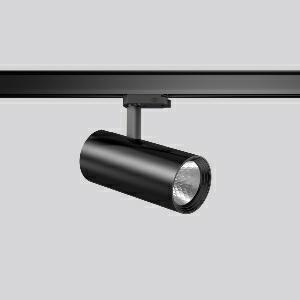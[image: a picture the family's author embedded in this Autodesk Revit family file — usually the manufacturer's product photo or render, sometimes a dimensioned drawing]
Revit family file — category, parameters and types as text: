
# Revit family: deecos_s_mini_742195_003_3_f3a6
name_source: partatom
category: Lighting Fixtures
units: mm (PartAtom-declared; Revit-internal decimal feet)

## family parameters
Cut with Voids When Loaded = No
Host = Face
Light Source = No
Part Type = Normal
Room Calculation Point = No
Round Connector Dimension = Use Diameter
Shared = No

## types (1)
- DEECOS S mini (1 x LED Modul 935, 2600 lm, 3500)
    Apparent Load = 20 VA
    Approval mark = CE
    CIE Flux Codes = 100 100 100 100 100
    Color Rendering = 92
    Color Temperature = 3500
    Default Elevation = 1800 mm
    Description = Series: DEECOS S mini
LED surface-mounted projector in modern design with no visible cooling ribs. Housing: die-cast aluminium, powder-coated. Rotation range: 356°. Swivel range: 90°. Black plastic ring and recessed LED to prevent glare from the side. Optical assembly with reflector made of MIRO-Silver with 98% total light reflection for outstanding efficiency - can be changed without tools. Best colour rendering index Ra>90. With multi adaptor for 3-circuit tracks 230 V. Suitable for Track on ceiling, Wall track. High quality converter without flickering and stroboscopic effect. The following accessories can be mounted without use of tools: interchangeable lenses, decorative glasses, honeycomb louvre, clear and frosted diffusers, white interchangeable plastic ring. 
Colour: deep black, matt (RAL 9005)
Diameter: 87 mm
Height: 214 mm
Lamp: LED
Socket: without socket
Colour temperature: 3500K
Colour rendering index (CRI): 92
System power: 20 W
Rated luminous flux: 2600 lm
Luminous efficiency: 130 lm/W
Control gear: Regulated power supply
Protection class: I
Type of protection: IP 20
    Height = 214 mm
    Lamp = 1 x LED Modul 935
    Lamp Light Flux = 2600 lm
    Lamp count = 1
    Length = 87 mm
    Lifetime = 50000 h
    Luminous efficacy = 130 lm/W
    Manufacturer = RZB
    ModVariant = No
    Model = 742195.003.3
    Mounting Place = Ceiling
    Mounting Type = Rail mounted
    Number of Poles = 1
    OnlyDefault = Yes
    Power Factor = 1
    Product Name = DEECOS S mini
    Product group = Track mounted projectors
    ProductGroupID = 301
    Protection Class = Protection class I
    Protection Degree = IP 20
    RLX_Detail_Level = 1
    RLX_Emergency_Light_Flux = 0 lm
    RLX_Emergency_Type = 0
    RLX_Emergency_Type_DB = No
    RlxData = <blob elided: 38705 chars, md5=fbb8870b>
    Socket = socket
    Standby Power = 0 W
    System Light Flux = 2600 lm
    System Power = 20 W
    Type Comments = Product without accessories
    Type Image = 741926.003.jpg
    URL = http://relux.com
    VarID = ---
    Voltage = 230 V
    Voltage Range = 220-240 V
    Weight = 0.00 kg
    Width = 0 mm  [stored 0 ft]

note: [stored X ft] marks values corroborated as IEEE doubles in the binary element streams (Revit-internal decimal feet)

## geometry (parser evidence)
native form markers: Blend x4, Sweep x12
no freeform markers — native parametric forms only
